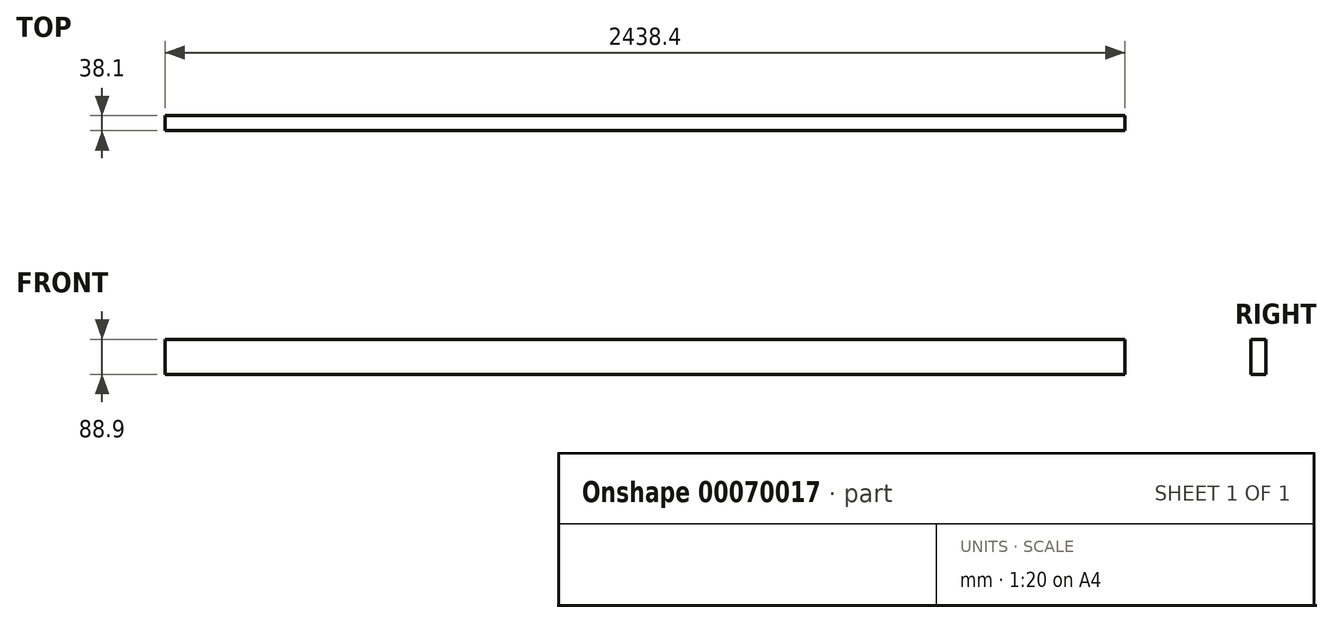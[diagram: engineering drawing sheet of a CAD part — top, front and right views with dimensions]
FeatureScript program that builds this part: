
annotation { "Feature Type Name" : "Feature", "Feature Type Description" : "" }
export const myFeature = defineFeature(function(context is Context, id is Id, definition is map)
    precondition{}
    {
        {
            var Q0;
            Q0=qCreatedBy(makeId("Top.planeOp"),FACE);
            var sketch = newSketch(context, id + "F0", { "sketchPlane" : qUnion([Q0])});
            skLineSegment(sketch, "E0.bottom", {"start": v(0, 0) * mm, "end": v(2438.4, 0) * mm});
            skLineSegment(sketch, "E0.top", {"start": v(0, 38.1) * mm, "end": v(2438.4, 38.1) * mm});
            skLineSegment(sketch, "E0.left", {"start": v(0, 0) * mm, "end": v(0, 38.1) * mm});
            skLineSegment(sketch, "E0.right", {"start": v(2438.4, 0) * mm, "end": v(2438.4, 38.1) * mm});
            skSolve(sketch);
        }
        {
            var Q0;
            Q0 = qSketchRegion(id + "F0", true);
            extrude(context, id + "F1", {"entities" : qUnion([Q0]), "depth" : 88.9 * mm});
        }
    });
